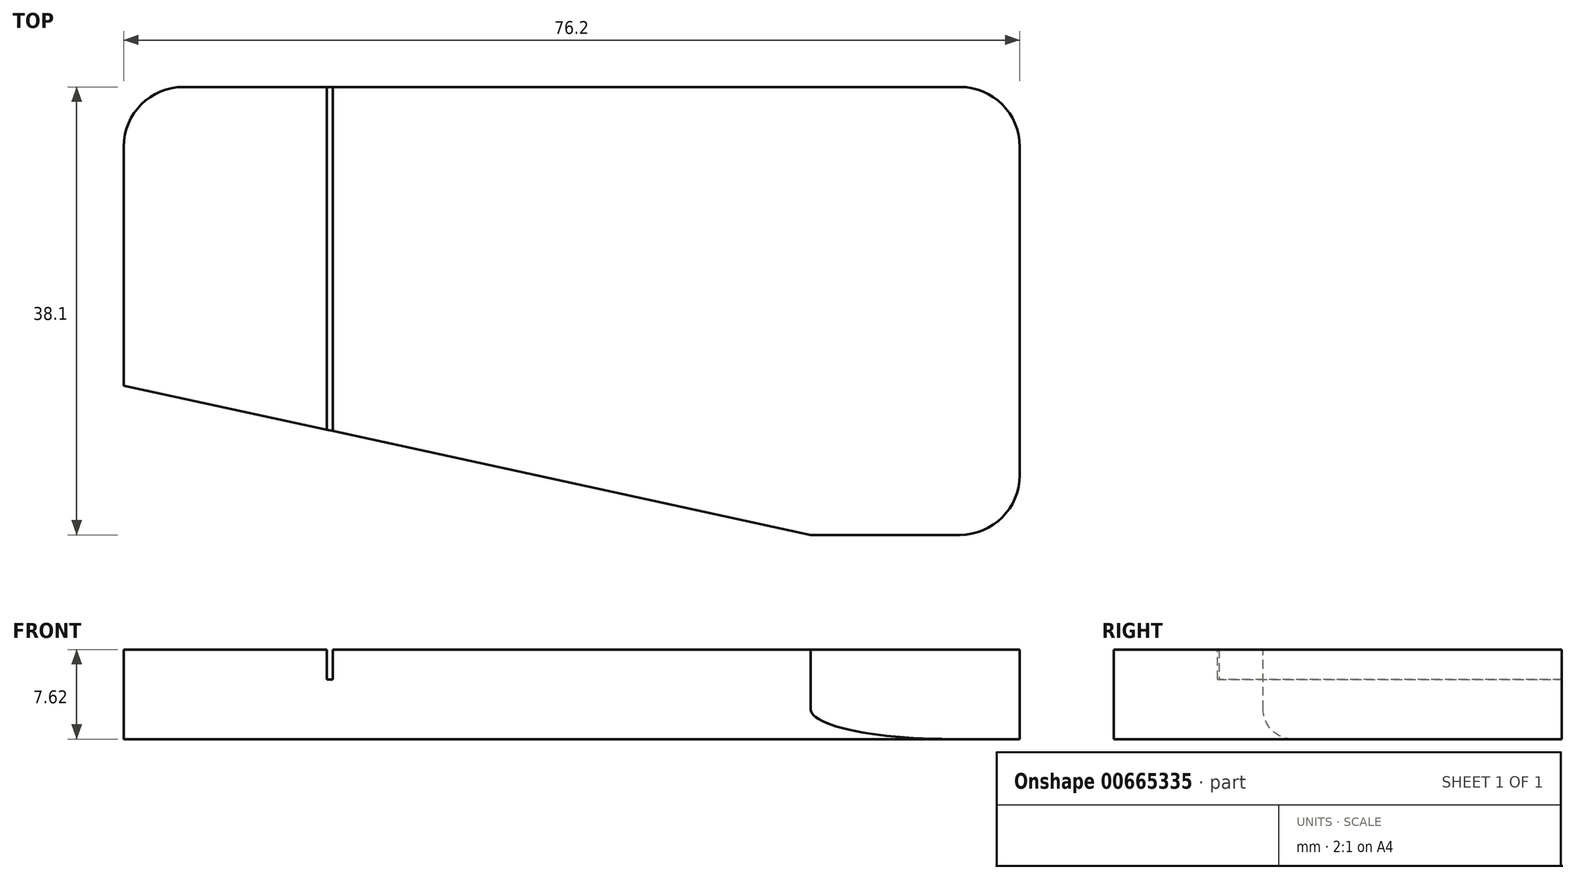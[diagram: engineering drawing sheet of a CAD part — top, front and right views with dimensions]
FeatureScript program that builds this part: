
annotation { "Feature Type Name" : "Feature", "Feature Type Description" : "" }
export const myFeature = defineFeature(function(context is Context, id is Id, definition is map)
    precondition{}
    {
        {
            var Q0;
            Q0=qCreatedBy(makeId("Top.planeOp"),FACE);
            var sketch = newSketch(context, id + "F0", { "sketchPlane" : qUnion([Q0])});
            skLineSegment(sketch, "E0.bottom", {"start": v(38.1, -19.05) * mm, "end": v(-38.1, -19.05) * mm});
            skLineSegment(sketch, "E0.top", {"start": v(38.1, 19.05) * mm, "end": v(-38.1, 19.05) * mm});
            skLineSegment(sketch, "E0.left", {"start": v(38.1, -19.05) * mm, "end": v(38.1, 19.05) * mm});
            skLineSegment(sketch, "E0.right", {"start": v(-38.1, -19.05) * mm, "end": v(-38.1, 19.05) * mm});
            skPoint(sketch, "E0.middle", {"position": v(0, 0) * mm});
            skSolve(sketch);
        }
        {
            var Q0;
            Q0=makeQuery(id+"F0.imprint","IMPRINT",FACE,{"disambiguationData":[TD([[makeQuery(id+"F0.imprint","IMPRINT",EDGE,{"derivedFrom":sQuery(id+"F0.wireOp",EDGE,"E0.bottom")}),-1.0]])]});
            extrude(context, id + "F1", {"entities" : qUnion([Q0]), "depth" : 7.62 * mm, "offsetDistance" : 25.4 * mm});
        }
        {
            var Q0;
            Q0=makeQuery(id+"F1.opExtrude","CAP_FACE",FACE,{"disambiguationData":[OSD([sQuery(id+"F0.wireOp",EDGE,"E0.bottom"),sQuery(id+"F0.wireOp",EDGE,"E0.top"),sQuery(id+"F0.wireOp",EDGE,"E0.left"),sQuery(id+"F0.wireOp",EDGE,"E0.right")])],"isStart":false});
            var sketch = newSketch(context, id + "F2", { "sketchPlane" : qUnion([Q0])});
            skLineSegment(sketch, "E1.bottom", {"start": v(20.32, -19.05) * mm, "end": v(-20.32, -19.05) * mm});
            skLineSegment(sketch, "E1.top", {"start": v(20.32, 19.05) * mm, "end": v(-20.32, 19.05) * mm});
            skLineSegment(sketch, "E1.left", {"start": v(20.32, -19.05) * mm, "end": v(20.32, 19.05) * mm});
            skLineSegment(sketch, "E1.right", {"start": v(-20.32, -19.05) * mm, "end": v(-20.32, 19.05) * mm});
            skPoint(sketch, "E1.middle", {"position": v(0, 0) * mm});
            skLineSegment(sketch, "E2.bottom", {"start": v(-20.32, 19.05) * mm, "end": v(-20.83, 19.05) * mm});
            skLineSegment(sketch, "E2.top", {"start": v(-20.32, -19.05) * mm, "end": v(-20.83, -19.05) * mm});
            skLineSegment(sketch, "E2.left", {"start": v(-20.32, 19.05) * mm, "end": v(-20.32, -19.05) * mm});
            skLineSegment(sketch, "E2.right", {"start": v(-20.83, 19.05) * mm, "end": v(-20.83, -19.05) * mm});
            skSolve(sketch);
        }
        {
            var Q0;
            {var subQ0=sQuery(id+"F2.wireOp",EDGE,"E1.left");Q0=makeQuery(id+"F2.imprint","IMPRINT",FACE,{"disambiguationData":[TD([[makeQuery(id+"F2.imprint","IMPRINT",EDGE,{"derivedFrom":subQ0}),-1.0]])]});}
            var sketch = newSketch(context, id + "F3", { "sketchPlane" : qUnion([Q0])});
            skLineSegment(sketch, "E3.0", {"start": v(-38.1, -19.05) * mm, "end": v(-38.1, 19.05) * mm});
            skLineSegment(sketch, "E4.0", {"start": v(20.32, -19.05) * mm, "end": v(-20.32, -19.05) * mm});
            skLineSegment(sketch, "E5.0", {"start": v(20.32, -19.05) * mm, "end": v(-38.1, -19.05) * mm});
            skPoint(sketch, "E6.orphan", {"position": v(38.1, -19.05) * mm});
            skLineSegment(sketch, "E7", {"start": v(-38.1, -6.35) * mm, "end": v(20.32, -19.05) * mm});
            skSolve(sketch);
        }
        {
            var Q0;
            {var subQ3=sQuery(id+"F3.wireOp",EDGE,"cd232530-1e49-4a57-8ab3-45a062eee770");Q0=makeQuery(id+"F3.imprint","IMPRINT",FACE,{"disambiguationData":[TD([[makeQuery(id+"F3.imprint","IMPRINT",EDGE,{"derivedFrom":subQ3}),-1.0]])]});}
            var Q1;
            {var subQ3=sQuery(id+"F3.wireOp",EDGE,"E7");Q1=makeQuery(id+"F3.imprint","IMPRINT",FACE,{"disambiguationData":[TD([[makeQuery(id+"F3.imprint","IMPRINT",EDGE,{"derivedFrom":subQ3}),-1.0]])]});}
            extrude(context, id + "F4", {"entities" : qUnion([Q0, Q1]), "operationType" : NewBodyOperationType.REMOVE, "endBound" : BoundingType.THROUGH_ALL, "oppositeDirection" : true, "depth" : 25.4 * mm, "offsetDistance" : 25.4 * mm});
        }
        {
            var Q0;
            Q0=makeQuery(id+"F4.boolean.opBoolean","COPY",EDGE,{"derivedFrom":makeQuery(id+"F4.opExtrude","SWEPT_EDGE",EDGE,{"disambiguationData":[OSD([sQuery(id+"F3.wireOp",EDGE,"E3.0"),sQuery(id+"F3.wireOp",EDGE,"cd232530-1e49-4a57-8ab3-45a062eee770")])]})});
            var Q1;
            Q1=makeQuery(id+"F1.opExtrude","SWEPT_EDGE",EDGE,{"disambiguationData":[OSD([sQuery(id+"F0.wireOp",EDGE,"E0.top"),sQuery(id+"F0.wireOp",EDGE,"E0.right")])]});
            var Q2;
            Q2=makeQuery(id+"F1.opExtrude","SWEPT_EDGE",EDGE,{"disambiguationData":[OSD([sQuery(id+"F0.wireOp",EDGE,"E0.bottom"),sQuery(id+"F0.wireOp",EDGE,"E0.left")])]});
            var Q3;
            Q3=makeQuery(id+"F1.opExtrude","SWEPT_EDGE",EDGE,{"disambiguationData":[OSD([sQuery(id+"F0.wireOp",EDGE,"E0.top"),sQuery(id+"F0.wireOp",EDGE,"E0.left")])]});
            var Q4;
            Q4=makeQuery(id+"F4.boolean.opBoolean","COPY",EDGE,{"derivedFrom":makeQuery(id+"F4.opExtrude","SWEPT_EDGE",EDGE,{"disambiguationData":[OSD([sQuery(id+"F0.wireOp",EDGE,"E0.bottom"),sQuery(id+"F2.wireOp",EDGE,"E1.left"),sQuery(id+"F3.wireOp",EDGE,"E5.0"),sQuery(id+"F3.wireOp",EDGE,"E7")])]})});
            fillet(context, id + "F5", {"entities" : qUnion([Q0, Q1, Q2, Q3, Q4]), "radius" : 5.08 * mm, "tangentPropagation" : true, "allowEdgeOverflow" : false});
        }
        {
            var Q0;
            Q0=makeQuery(id+"F4.boolean.opBoolean","COPY",EDGE,{"derivedFrom":makeQuery(id+"F4.opExtrude","CAP_EDGE",EDGE,{"disambiguationData":[OSD([sQuery(id+"F3.wireOp",EDGE,"E7")])],"isStart":true})});
            var Q1;
            Q1=makeQuery(id+"F4.boolean.opBoolean","INTERSECT",EDGE,{"derivedFrom":[makeQuery(id+"F1.opExtrude","CAP_FACE",FACE,{"disambiguationData":[OSD([sQuery(id+"F0.wireOp",EDGE,"E0.bottom"),sQuery(id+"F0.wireOp",EDGE,"E0.top"),sQuery(id+"F0.wireOp",EDGE,"E0.left"),sQuery(id+"F0.wireOp",EDGE,"E0.right")])],"isStart":true}),makeQuery(id+"F4.opExtrude","SWEPT_FACE",FACE,{"disambiguationData":[OSD([sQuery(id+"F3.wireOp",EDGE,"E7")])]})]});
            fillet(context, id + "F6", {"entities" : qUnion([Q0, Q1]), "radius" : 2.54 * mm, "tangentPropagation" : true, "allowEdgeOverflow" : false});
        }
        {
            var Q0;
            Q0=makeQuery(id+"F2.imprint","IMPRINT",FACE,{"disambiguationData":[TD([[makeQuery(id+"F2.imprint","IMPRINT",EDGE,{"derivedFrom":sQuery(id+"F2.wireOp",EDGE,"E2.bottom")}),1.0]])]});
            extrude(context, id + "F7", {"entities" : qUnion([Q0]), "operationType" : NewBodyOperationType.REMOVE, "oppositeDirection" : true, "depth" : 2.54 * mm, "offsetDistance" : 25.4 * mm});
        }
    });
